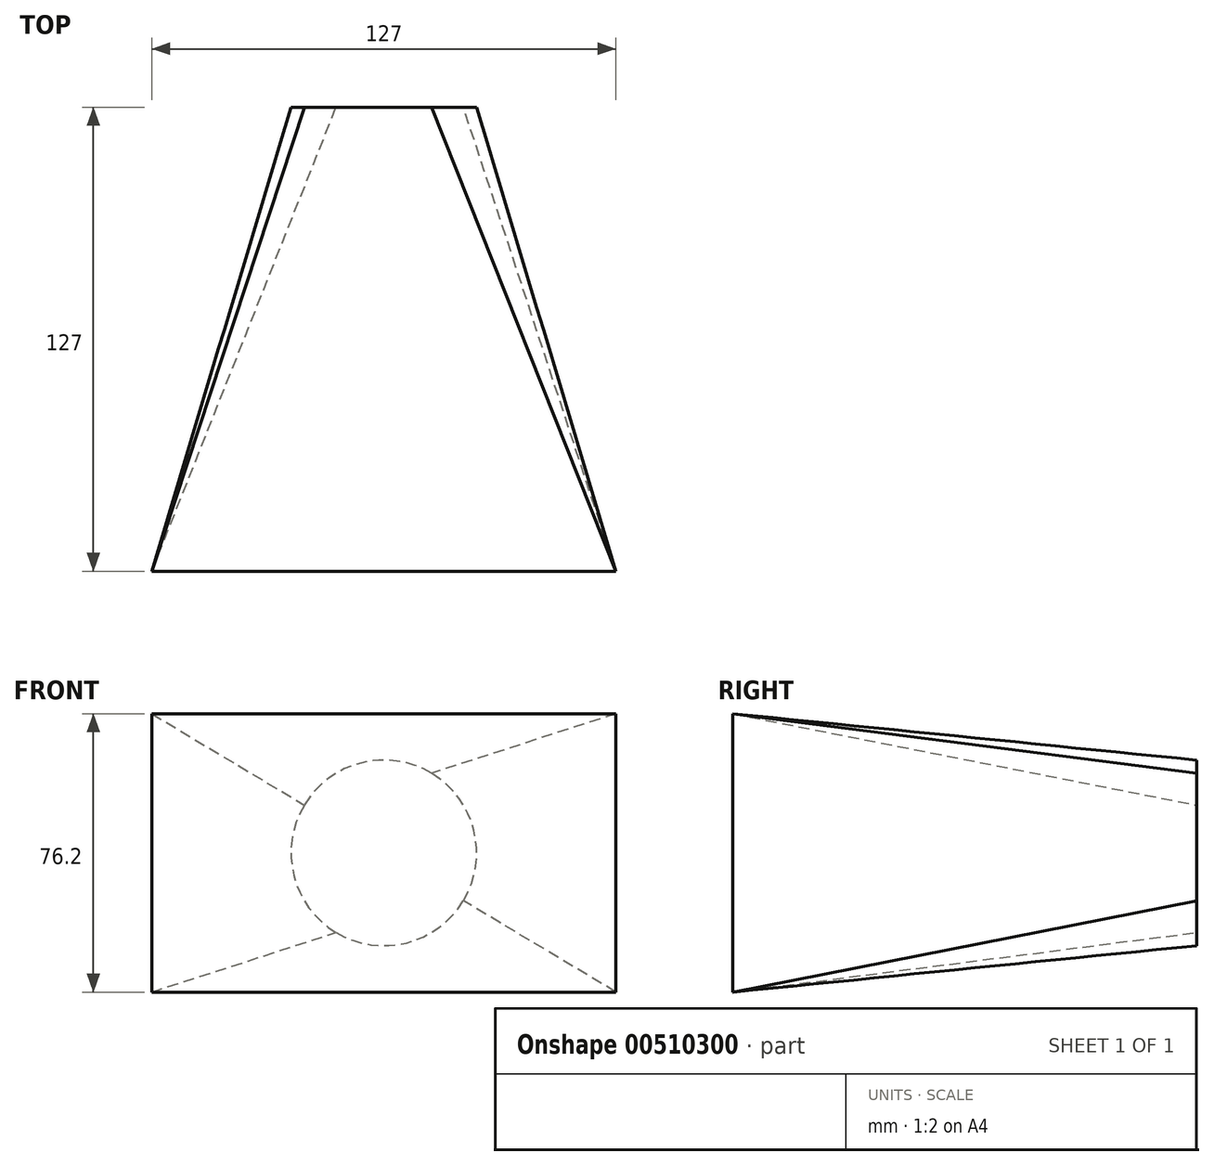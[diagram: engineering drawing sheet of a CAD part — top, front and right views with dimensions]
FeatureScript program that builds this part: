
annotation { "Feature Type Name" : "Feature", "Feature Type Description" : "" }
export const myFeature = defineFeature(function(context is Context, id is Id, definition is map)
    precondition{}
    {
        {
            var Q0;
            Q0=qCreatedBy(makeId("Front.planeOp"),FACE);
            var sketch = newSketch(context, id + "F0", { "sketchPlane" : qUnion([Q0])});
            skCircle(sketch, "E0", {"center": v(0, 0) * mm, "radius": 25.4 * mm});
            skSolve(sketch);
        }
        {
            var Q0;
            Q0=qCreatedBy(makeId("Front.planeOp"),FACE);
            cPlane(context, id + "F1", {"entities" : qUnion([Q0]), "cplaneType" : CPlaneType.OFFSET, "offset" : 127 * mm, "width" : 152.4 * mm, "height" : 152.4 * mm});
        }
        {
            var Q0;
            Q0=qCreatedBy(id+"F1.planeOp",FACE);
            var sketch = newSketch(context, id + "F2", { "sketchPlane" : qUnion([Q0])});
            skLineSegment(sketch, "E1.bottom", {"start": v(-63.5, 38.1) * mm, "end": v(63.5, 38.1) * mm});
            skLineSegment(sketch, "E1.top", {"start": v(-63.5, -38.1) * mm, "end": v(63.5, -38.1) * mm});
            skLineSegment(sketch, "E1.left", {"start": v(-63.5, 38.1) * mm, "end": v(-63.5, -38.1) * mm});
            skLineSegment(sketch, "E1.right", {"start": v(63.5, 38.1) * mm, "end": v(63.5, -38.1) * mm});
            skPoint(sketch, "E1.middle", {"position": v(0, 0) * mm});
            skSolve(sketch);
        }
        {
            var Q0;
            Q0=makeQuery(id+"F2.imprint","IMPRINT",FACE,{"disambiguationData":[TD([[makeQuery(id+"F2.imprint","IMPRINT",EDGE,{"derivedFrom":sQuery(id+"F2.wireOp",EDGE,"E1.bottom")}),-1.0]])]});
            var Q1;
            Q1=makeQuery(id+"F0.imprint","IMPRINT",FACE,{"disambiguationData":[TD([[makeQuery(id+"F0.imprint","IMPRINT",EDGE,{"derivedFrom":sQuery(id+"F0.wireOp",EDGE,"E0")}),1.0]])]});
            loft(context, id + "F3", {"sheetProfilesArray" : [{ "sheetProfileEntities" : qUnion([Q0]) }, { "sheetProfileEntities" : qUnion([Q1]) }]});
        }
    });
